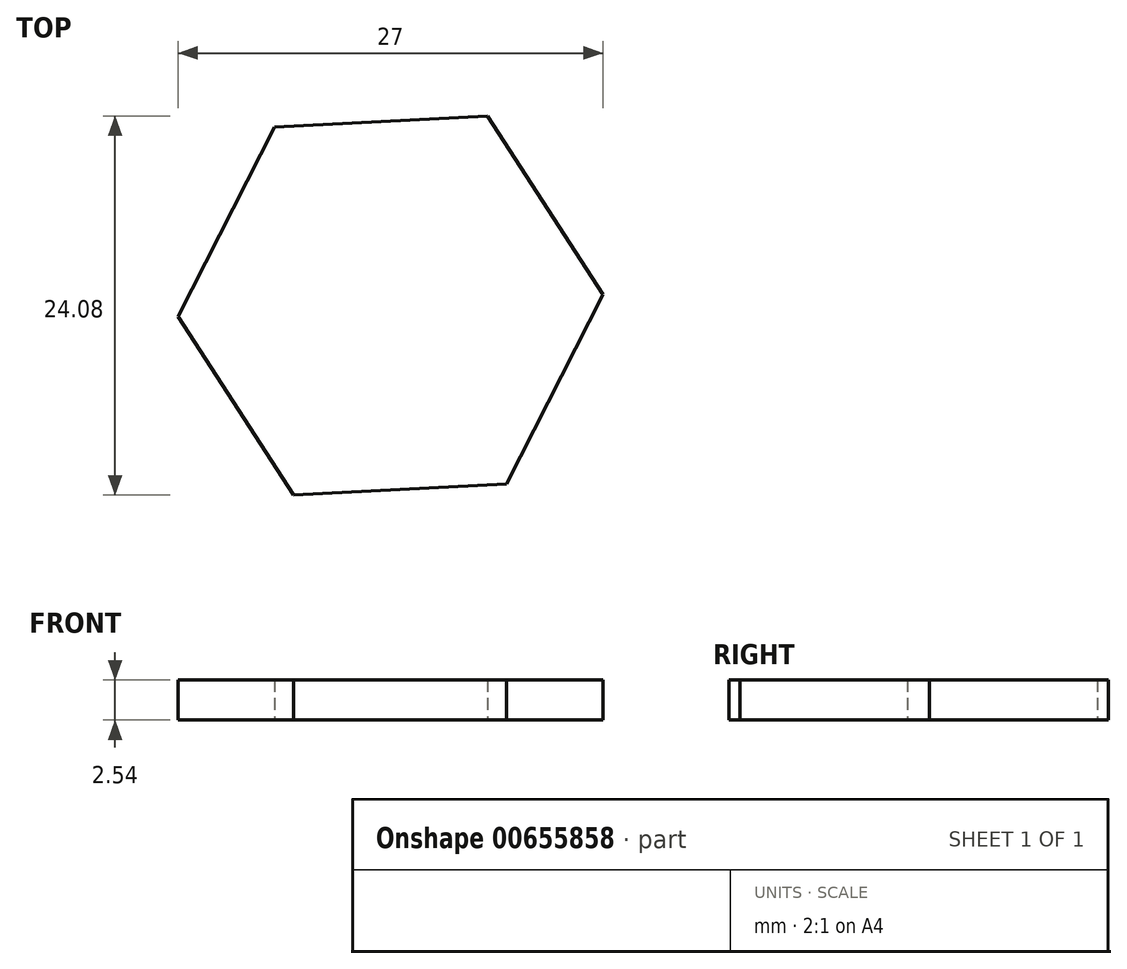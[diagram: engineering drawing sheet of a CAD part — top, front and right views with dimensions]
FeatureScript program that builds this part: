
annotation { "Feature Type Name" : "Feature", "Feature Type Description" : "" }
export const myFeature = defineFeature(function(context is Context, id is Id, definition is map)
    precondition{}
    {
        {
            var Q0;
            Q0=qCreatedBy(makeId("Top.planeOp"),FACE);
            var sketch = newSketch(context, id + "F0", { "sketchPlane" : qUnion([Q0])});
            skCircle(sketch, "E0.cCircle", {"center": v(0, 0) * mm, "radius": 11.7 * mm, "construction": true});
            skLineSegment(sketch, "E0.0", {"start": v(-6.15, -12.04) * mm, "end": v(-13.5, -0.7) * mm});
            skLineSegment(sketch, "E0.1", {"start": v(-13.5, -0.7) * mm, "end": v(-7.36, 11.35) * mm});
            skLineSegment(sketch, "E0.2", {"start": v(-7.36, 11.35) * mm, "end": v(6.15, 12.04) * mm});
            skLineSegment(sketch, "E0.3", {"start": v(6.15, 12.04) * mm, "end": v(13.5, 0.7) * mm});
            skLineSegment(sketch, "E0.4", {"start": v(13.5, 0.7) * mm, "end": v(7.36, -11.35) * mm});
            skLineSegment(sketch, "E0.5", {"start": v(7.36, -11.35) * mm, "end": v(-6.15, -12.04) * mm});
            skPoint(sketch, "E0.0.midPoint", {"position": v(-9.83, -6.37) * mm});
            skSolve(sketch);
        }
        {
            var Q0;
            Q0 = qSketchRegion(id + "F0", true);
            extrude(context, id + "F1", {"entities" : qUnion([Q0]), "depth" : 2.54 * mm, "offsetDistance" : 25.4 * mm});
        }
    });
